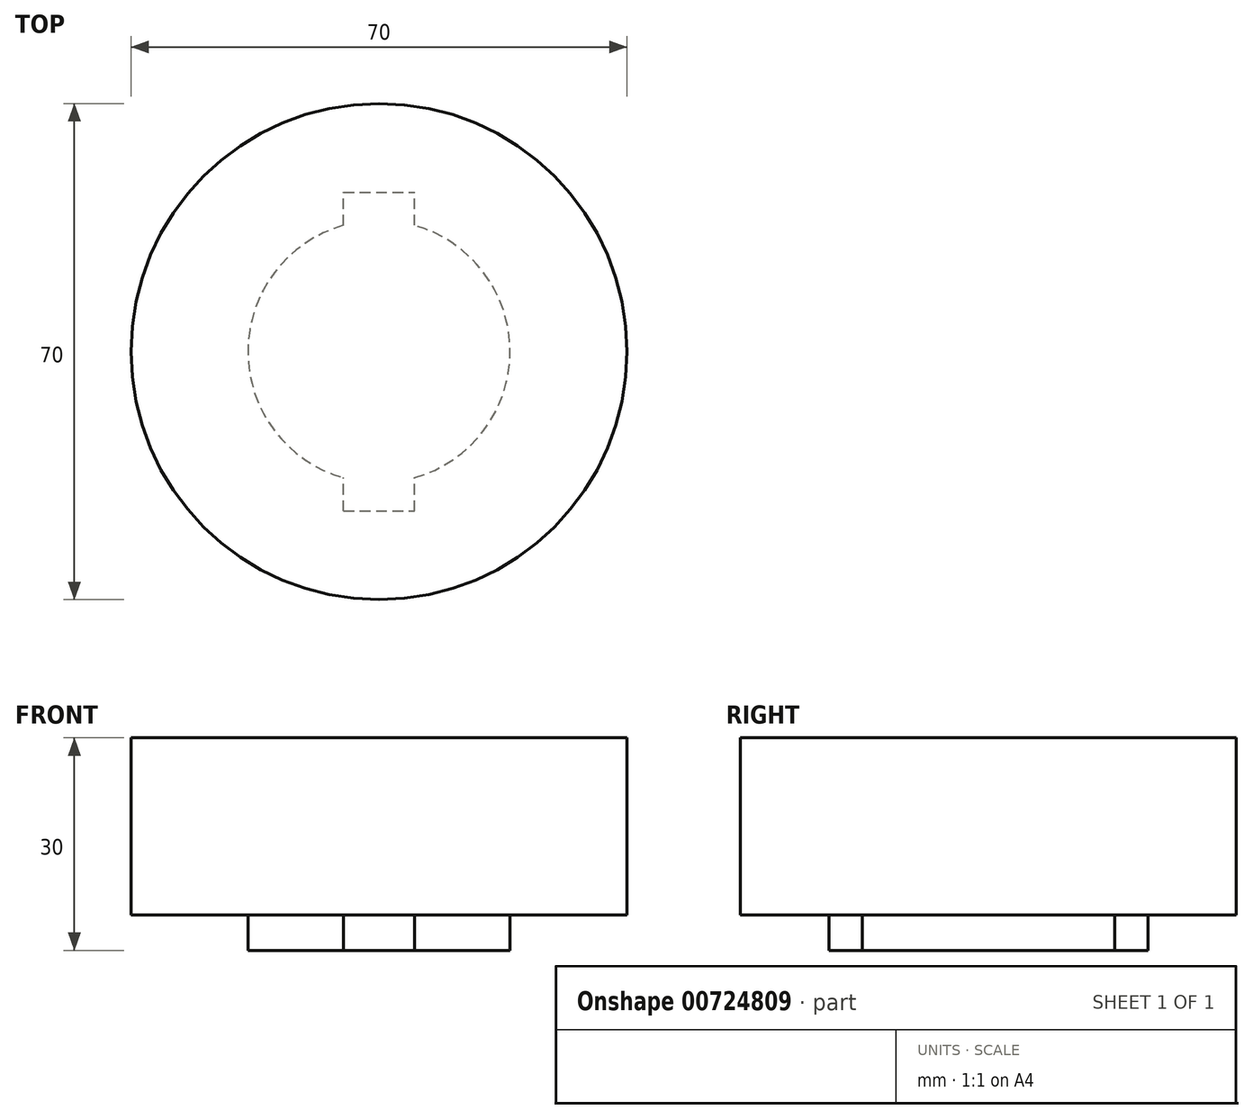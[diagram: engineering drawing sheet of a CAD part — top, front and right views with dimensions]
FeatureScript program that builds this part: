
annotation { "Feature Type Name" : "Feature", "Feature Type Description" : "" }
export const myFeature = defineFeature(function(context is Context, id is Id, definition is map)
    precondition{}
    {
        {
            var Q0;
            Q0=qCreatedBy(makeId("Top.planeOp"),FACE);
            var sketch = newSketch(context, id + "F0", { "sketchPlane" : qUnion([Q0])});
            skCircle(sketch, "E0", {"center": v(0, 0) * mm, "radius": 35 * mm});
            skSolve(sketch);
        }
        {
            var Q0;
            Q0=makeQuery(id+"F0.imprint","IMPRINT",FACE,{"disambiguationData":[TD([[makeQuery(id+"F0.imprint","IMPRINT",EDGE,{"derivedFrom":sQuery(id+"F0.wireOp",EDGE,"E0")}),1.0]])]});
            extrude(context, id + "F1", {"entities" : qUnion([Q0]), "depth" : 25 * mm, "offsetDistance" : 25 * mm});
        }
        {
            var Q0;
            Q0=makeQuery(id+"F1.opExtrude","CAP_FACE",FACE,{"disambiguationData":[OSD([sQuery(id+"F0.wireOp",EDGE,"E0")])],"isStart":true});
            var sketch = newSketch(context, id + "F2", { "sketchPlane" : qUnion([Q0])});
            skArc(sketch, "E1", {"start": v(-5, 17.81) * mm, "mid": v(-18.5, 0) * mm, "end": v(-5, -17.81) * mm});
            skLineSegment(sketch, "E2.bottom", {"start": v(-5, 22.5) * mm, "end": v(5, 22.5) * mm});
            skLineSegment(sketch, "E2.top", {"start": v(-5, -22.5) * mm, "end": v(5, -22.5) * mm});
            skLineSegment(sketch, "E2.left", {"start": v(-5, 22.5) * mm, "end": v(-5, 17.81) * mm});
            skLineSegment(sketch, "E2.right", {"start": v(5, 22.5) * mm, "end": v(5, 17.81) * mm});
            skLineSegment(sketch, "E3", {"start": v(0, 0) * mm, "end": v(-5, 0) * mm, "construction": true});
            skLineSegment(sketch, "E4", {"start": v(0, 22.5) * mm, "end": v(0, 0) * mm, "construction": true});
            skLineSegment(sketch, "E5.trimOffspring", {"start": v(-5, -17.81) * mm, "end": v(-5, -22.5) * mm});
            skArc(sketch, "E6.trimOffspring", {"start": v(5, -17.81) * mm, "mid": v(18.5, 0) * mm, "end": v(5, 17.81) * mm});
            skLineSegment(sketch, "E7.trimOffspring", {"start": v(5, -17.81) * mm, "end": v(5, -22.5) * mm});
            skSolve(sketch);
        }
        {
            var Q0;
            Q0 = qSketchRegion(id + "F2", true);
            extrude(context, id + "F3", {"entities" : qUnion([Q0]), "operationType" : NewBodyOperationType.ADD, "depth" : 5 * mm, "offsetDistance" : 25 * mm});
        }
    });
